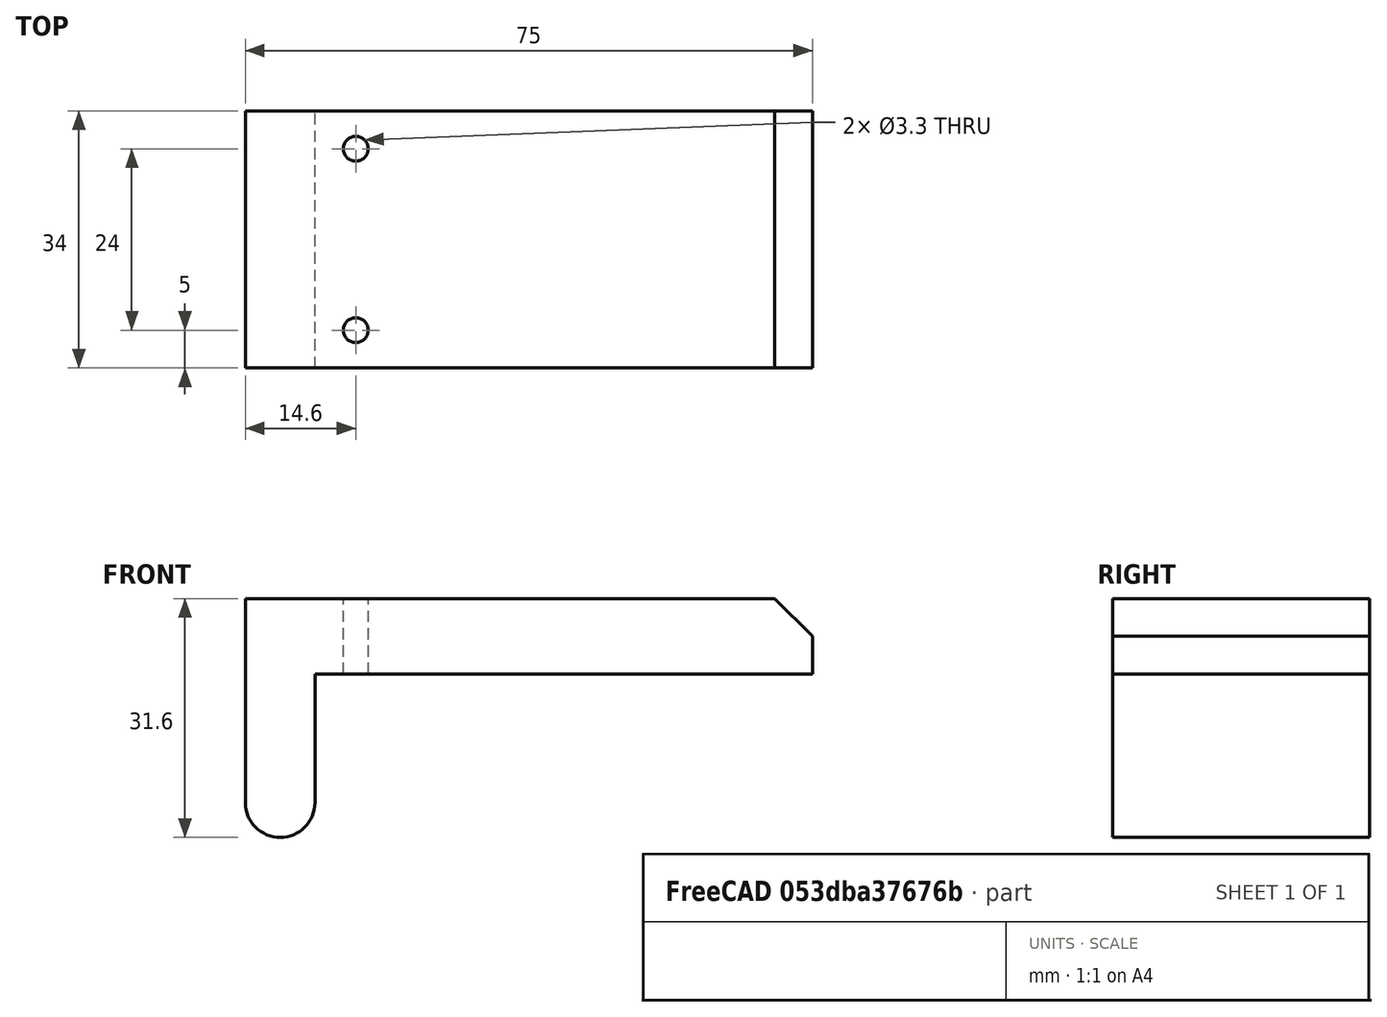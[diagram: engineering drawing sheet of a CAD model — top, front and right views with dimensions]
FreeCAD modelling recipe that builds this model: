
FCSTD DOCUMENT  (FreeCAD 0.15R4671 (Git))
Label: table_mount_bottom
License: All rights reserved
LicenseURL: http://en.wikipedia.org/wiki/All_rights_reserved
objects: Part::Cylinder×3, Part::Box×2, Part::MultiFuse×2, Part::Cut×1, Part::Chamfer×1
note: 9 computed .brp shape members not serialized (recipe doc carries the construction recipe); baked Part::Feature solids carry a one-line shape summary decoded from their .brp

FEATURE [Part::Cylinder] Cylinder
  Angle = 360
  Height = 34
  Placement = pos=(0,0,0) rot=(-1,0,0;1.5708rad)
  Radius = 4.6
FEATURE [Part::Box] Box  label="Cube"
  Height = 17
  Length = 9.2
  Placement = pos=(-4.6,0,0) rot=(0,0,1;0rad)
  Width = 34
FEATURE [Part::Box] Box001  label="Cube001"
  Height = 10
  Length = 75
  Placement = pos=(-4.6,0,17) rot=(0,0,1;0rad)
  Width = 34
FEATURE [Part::Cylinder] Cylinder001
  Angle = 360
  Height = 20
  Placement = pos=(10,5,7) rot=(0,0,1;0rad)
  Radius = 1.65
FEATURE [Part::Cylinder] Cylinder002
  Angle = 360
  Height = 20
  Placement = pos=(10,29,7) rot=(0,0,1;0rad)
  Radius = 1.65
FEATURE [Part::MultiFuse] Fusion001
  Shapes = -> [Cylinder002,Cylinder001]
FEATURE [Part::MultiFuse] Fusion
  Shapes = -> [Cylinder,Box001,Box]
FEATURE [Part::Cut] Cut
  Base = -> Fusion
  Tool = -> Fusion001
FEATURE [Part::Chamfer] Chamfer
  Base = -> Cut
  Edges = 1 edges r=5: [Edge4]
